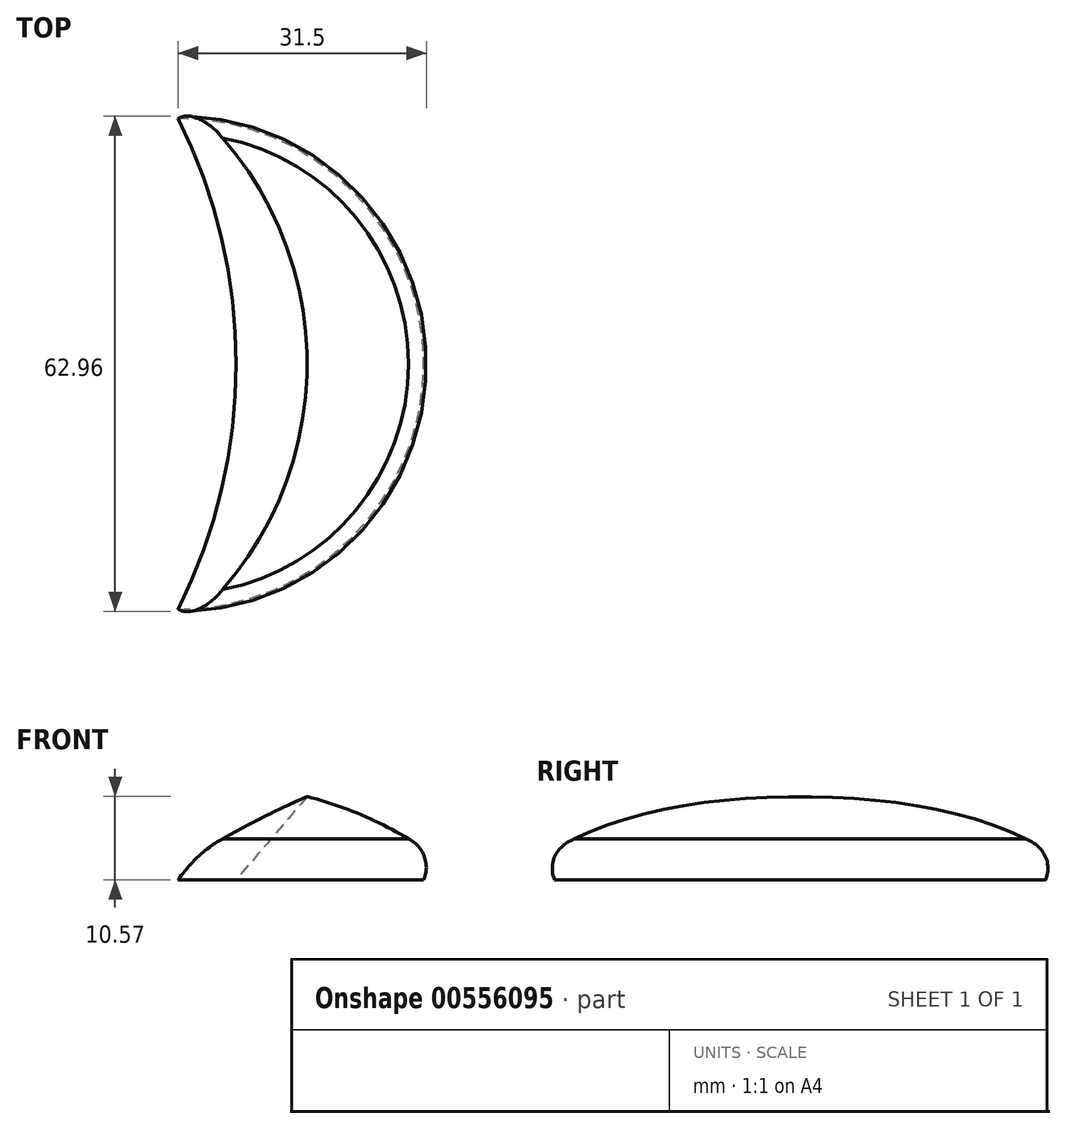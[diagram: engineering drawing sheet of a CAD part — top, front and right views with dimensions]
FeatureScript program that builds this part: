
annotation { "Feature Type Name" : "Feature", "Feature Type Description" : "" }
export const myFeature = defineFeature(function(context is Context, id is Id, definition is map)
    precondition{}
    {
        {
            var Q0;
            Q0=qCreatedBy(makeId("Front.planeOp"),FACE);
            var sketch = newSketch(context, id + "F0", { "sketchPlane" : qUnion([Q0])});
            skLineSegment(sketch, "E0", {"start": v(0, 0) * mm, "end": v(0, 11.62) * mm});
            skArc(sketch, "E1", {"start": v(29.23, 5.2) * mm, "mid": v(15.15, 10.85) * mm, "end": v(0, 11.62) * mm});
            skArc(sketch, "E2", {"start": v(31.17, 0) * mm, "mid": v(31.25, 2.99) * mm, "end": v(29.23, 5.2) * mm});
            skLineSegment(sketch, "E3", {"start": v(0, 0) * mm, "end": v(31.17, 0) * mm});
            skSolve(sketch);
        }
        {
            var Q0;
            Q0 = qSketchRegion(id + "F0", true);
            var Q1;
            Q1=sQuery(id+"F0.wireOp",EDGE,"E0");
            revolve(context, id + "F1", {"entities" : qUnion([Q0]), "axis" : qUnion([Q1]), "revolveType" : RevolveType.FULL});
        }
        {
            var Q0;
            Q0=qCreatedBy(makeId("Front.planeOp"),FACE);
            var sketch = newSketch(context, id + "F2", { "sketchPlane" : qUnion([Q0])});
            skLineSegment(sketch, "E4", {"start": v(0, 0) * mm, "end": v(0, 15) * mm, "construction": true});
            skLineSegment(sketch, "E5", {"start": v(-7.5, 15) * mm, "end": v(7.5, 15) * mm});
            skLineSegment(sketch, "E6", {"start": v(7.5, 15) * mm, "end": v(0, 0) * mm});
            skLineSegment(sketch, "E7", {"start": v(-7.5, 15) * mm, "end": v(0, 0) * mm});
            skSolve(sketch);
        }
        {
            var Q0;
            Q0 = qSketchRegion(id + "F2", true);
            extrude(context, id + "F3", {"entities" : qUnion([Q0]), "operationType" : NewBodyOperationType.REMOVE, "endBound" : BoundingType.THROUGH_ALL, "oppositeDirection" : true, "depth" : 25 * mm, "offsetDistance" : 25 * mm, "hasSecondDirection" : true, "secondDirectionBound" : SecondDirectionBoundingType.THROUGH_ALL, "secondDirectionOppositeDirection" : false, "secondDirectionDepth" : 25 * mm});
        }
        {
            var Q0;
            Q0=qCreatedBy(makeId("Top.planeOp"),FACE);
            var sketch = newSketch(context, id + "F4", { "sketchPlane" : qUnion([Q0])});
            skCircle(sketch, "E8", {"center": v(-62.68, 0) * mm, "radius": 70 * mm});
            skPoint(sketch, "E9.0", {"position": v(0, 31.17) * mm});
            skSolve(sketch);
        }
        {
            var Q0;
            Q0=qCreatedBy(makeId("Top.planeOp"),FACE);
            cPlane(context, id + "F5", {"entities" : qUnion([Q0]), "cplaneType" : CPlaneType.OFFSET, "offset" : 25 * mm, "width" : 150 * mm, "height" : 150 * mm});
        }
        {
            var Q0;
            Q0=qCreatedBy(id+"F5.planeOp",FACE);
            var sketch = newSketch(context, id + "F6", { "sketchPlane" : qUnion([Q0])});
            skCircle(sketch, "E10", {"center": v(-41.32, 0) * mm, "radius": 70 * mm});
            skSolve(sketch);
        }
        {
            var Q0;
            Q0=makeQuery(id+"F4.imprint","IMPRINT",FACE,{"disambiguationData":[TD([[makeQuery(id+"F4.imprint","IMPRINT",EDGE,{"derivedFrom":sQuery(id+"F4.wireOp",EDGE,"E8")}),1.0]])]});
            var Q1;
            Q1=makeQuery(id+"F6.imprint","IMPRINT",FACE,{"disambiguationData":[TD([[makeQuery(id+"F6.imprint","IMPRINT",EDGE,{"derivedFrom":sQuery(id+"F6.wireOp",EDGE,"E10")}),1.0]])]});
            loft(context, id + "F7", {"operationType" : NewBodyOperationType.REMOVE, "sheetProfilesArray" : [{ "sheetProfileEntities" : qUnion([Q0]) }, { "sheetProfileEntities" : qUnion([Q1]) }]});
        }
    });
